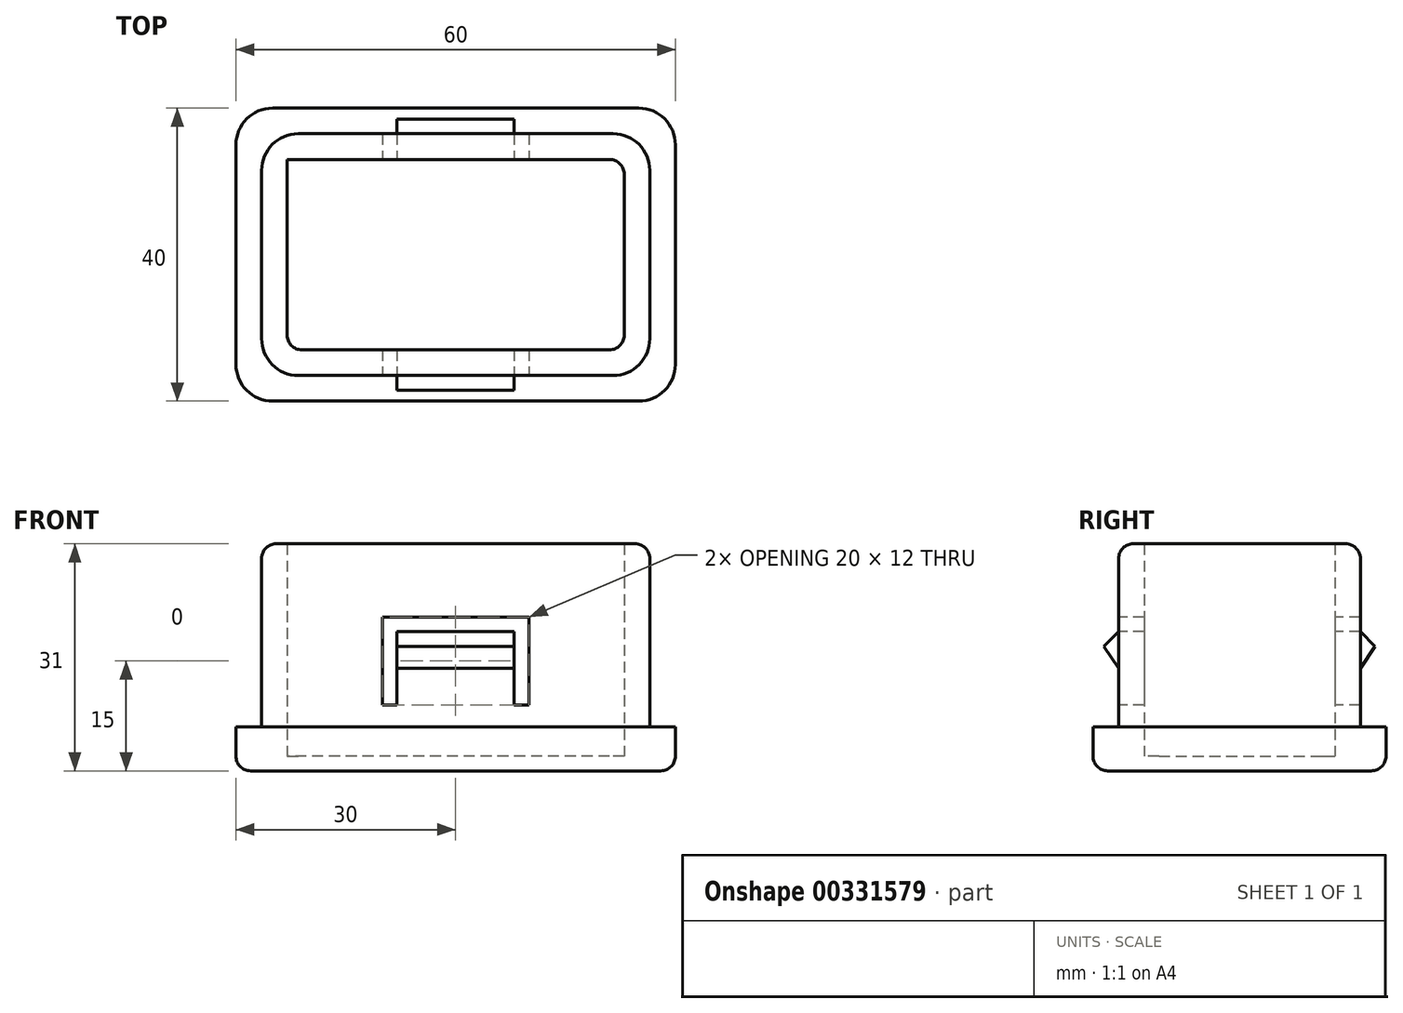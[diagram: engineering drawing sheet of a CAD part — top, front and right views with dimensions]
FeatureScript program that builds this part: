
annotation { "Feature Type Name" : "Feature", "Feature Type Description" : "" }
export const myFeature = defineFeature(function(context is Context, id is Id, definition is map)
    precondition{}
    {
        {
            var Q0;
            Q0=qCreatedBy(makeId("Top.planeOp"),FACE);
            var sketch = newSketch(context, id + "F0", { "sketchPlane" : qUnion([Q0])});
            skLineSegment(sketch, "E0.bottom", {"start": v(30, -20) * mm, "end": v(-30, -20) * mm});
            skLineSegment(sketch, "E0.top", {"start": v(30, 20) * mm, "end": v(-30, 20) * mm});
            skLineSegment(sketch, "E0.left", {"start": v(30, -20) * mm, "end": v(30, 20) * mm});
            skLineSegment(sketch, "E0.right", {"start": v(-30, -20) * mm, "end": v(-30, 20) * mm});
            skPoint(sketch, "E0.middle", {"position": v(0, 0) * mm});
            skSolve(sketch);
        }
        {
            var Q0;
            Q0 = qSketchRegion(id + "F0", true);
            extrude(context, id + "F1", {"entities" : qUnion([Q0]), "depth" : 2 * mm});
        }
        {
            var Q0;
            Q0=makeQuery(id+"F1.opExtrude","CAP_FACE",FACE,{"disambiguationData":[OSD([sQuery(id+"F0.wireOp",EDGE,"E0.bottom"),sQuery(id+"F0.wireOp",EDGE,"E0.top"),sQuery(id+"F0.wireOp",EDGE,"E0.left"),sQuery(id+"F0.wireOp",EDGE,"E0.right")])],"isStart":false});
            var sketch = newSketch(context, id + "F2", { "sketchPlane" : qUnion([Q0])});
            skLineSegment(sketch, "E1.0", {"start": v(30, 20) * mm, "end": v(-30, 20) * mm});
            skLineSegment(sketch, "E1.1", {"start": v(-30, -20) * mm, "end": v(-30, 20) * mm});
            skLineSegment(sketch, "E1.2", {"start": v(30, -20) * mm, "end": v(-30, -20) * mm});
            skLineSegment(sketch, "E1.3", {"start": v(30, -20) * mm, "end": v(30, 20) * mm});
            skLineSegment(sketch, "E2.0", {"start": v(-23, -13) * mm, "end": v(-23, 13) * mm});
            skLineSegment(sketch, "E2.1", {"start": v(23, -13) * mm, "end": v(-23, -13) * mm});
            skLineSegment(sketch, "E2.2", {"start": v(23, -13) * mm, "end": v(23, 13) * mm});
            skLineSegment(sketch, "E2.3", {"start": v(23, 13) * mm, "end": v(-23, 13) * mm});
            skSolve(sketch);
        }
        {
            var Q0;
            Q0 = qSketchRegion(id + "F2", true);
            extrude(context, id + "F3", {"entities" : qUnion([Q0]), "operationType" : NewBodyOperationType.ADD, "depth" : 4 * mm});
        }
        {
            var Q0;
            Q0=makeQuery(id+"F3.opExtrude","CAP_FACE",FACE,{"disambiguationData":[OSD([sQuery(id+"F2.wireOp",EDGE,"E1.0"),sQuery(id+"F2.wireOp",EDGE,"E1.1"),sQuery(id+"F2.wireOp",EDGE,"E1.2"),sQuery(id+"F2.wireOp",EDGE,"E1.3"),sQuery(id+"F2.wireOp",EDGE,"E2.0"),sQuery(id+"F2.wireOp",EDGE,"E2.1"),sQuery(id+"F2.wireOp",EDGE,"E2.2"),sQuery(id+"F2.wireOp",EDGE,"E2.3")])],"isStart":false});
            var sketch = newSketch(context, id + "F4", { "sketchPlane" : qUnion([Q0])});
            skLineSegment(sketch, "E3.0", {"start": v(23, 13) * mm, "end": v(-23, 13) * mm});
            skLineSegment(sketch, "E3.1", {"start": v(23, -13) * mm, "end": v(23, 13) * mm});
            skLineSegment(sketch, "E3.2", {"start": v(23, -13) * mm, "end": v(-23, -13) * mm});
            skLineSegment(sketch, "E3.3", {"start": v(-23, -13) * mm, "end": v(-23, 13) * mm});
            skLineSegment(sketch, "E4.0", {"start": v(26.5, 16.5) * mm, "end": v(-26.5, 16.5) * mm});
            skLineSegment(sketch, "E4.1", {"start": v(26.5, -16.5) * mm, "end": v(26.5, 16.5) * mm});
            skLineSegment(sketch, "E4.2", {"start": v(26.5, -16.5) * mm, "end": v(-26.5, -16.5) * mm});
            skLineSegment(sketch, "E4.3", {"start": v(-26.5, -16.5) * mm, "end": v(-26.5, 16.5) * mm});
            skSolve(sketch);
        }
        {
            var Q0;
            Q0 = qSketchRegion(id + "F4", true);
            extrude(context, id + "F5", {"entities" : qUnion([Q0]), "operationType" : NewBodyOperationType.ADD, "depth" : 25 * mm});
        }
        {
            var Q0;
            Q0=makeQuery(id+"F5.opExtrude","SWEPT_EDGE",EDGE,{"disambiguationData":[OSD([sQuery(id+"F4.wireOp",EDGE,"E4.2"),sQuery(id+"F4.wireOp",EDGE,"E4.3")])]});
            var Q1;
            Q1=makeQuery(id+"F5.opExtrude","SWEPT_EDGE",EDGE,{"disambiguationData":[OSD([sQuery(id+"F4.wireOp",EDGE,"E4.1"),sQuery(id+"F4.wireOp",EDGE,"E4.2")])]});
            var Q2;
            Q2=makeQuery(id+"F5.opExtrude","SWEPT_EDGE",EDGE,{"disambiguationData":[OSD([sQuery(id+"F4.wireOp",EDGE,"E4.0"),sQuery(id+"F4.wireOp",EDGE,"E4.3")])]});
            var Q3;
            Q3=makeQuery(id+"F3.boolean.opBoolean","MERGE",EDGE,{"derivedFrom":[makeQuery(id+"F1.opExtrude","SWEPT_EDGE",EDGE,{"disambiguationData":[OSD([sQuery(id+"F0.wireOp",EDGE,"E0.bottom"),sQuery(id+"F0.wireOp",EDGE,"E0.right")])]}),makeQuery(id+"F3.opExtrude","SWEPT_EDGE",EDGE,{"disambiguationData":[OSD([sQuery(id+"F2.wireOp",EDGE,"E1.1"),sQuery(id+"F2.wireOp",EDGE,"E1.2")])]})]});
            var Q4;
            Q4=makeQuery(id+"F3.boolean.opBoolean","MERGE",EDGE,{"derivedFrom":[makeQuery(id+"F1.opExtrude","SWEPT_EDGE",EDGE,{"disambiguationData":[OSD([sQuery(id+"F0.wireOp",EDGE,"E0.bottom"),sQuery(id+"F0.wireOp",EDGE,"E0.left")])]}),makeQuery(id+"F3.opExtrude","SWEPT_EDGE",EDGE,{"disambiguationData":[OSD([sQuery(id+"F2.wireOp",EDGE,"E1.2"),sQuery(id+"F2.wireOp",EDGE,"E1.3")])]})]});
            var Q5;
            Q5=makeQuery(id+"F3.boolean.opBoolean","MERGE",EDGE,{"derivedFrom":[makeQuery(id+"F1.opExtrude","SWEPT_EDGE",EDGE,{"disambiguationData":[OSD([sQuery(id+"F0.wireOp",EDGE,"E0.top"),sQuery(id+"F0.wireOp",EDGE,"E0.right")])]}),makeQuery(id+"F3.opExtrude","SWEPT_EDGE",EDGE,{"disambiguationData":[OSD([sQuery(id+"F2.wireOp",EDGE,"E1.0"),sQuery(id+"F2.wireOp",EDGE,"E1.1")])]})]});
            var Q6;
            Q6=makeQuery(id+"F3.boolean.opBoolean","MERGE",EDGE,{"derivedFrom":[makeQuery(id+"F1.opExtrude","SWEPT_EDGE",EDGE,{"disambiguationData":[OSD([sQuery(id+"F0.wireOp",EDGE,"E0.top"),sQuery(id+"F0.wireOp",EDGE,"E0.left")])]}),makeQuery(id+"F3.opExtrude","SWEPT_EDGE",EDGE,{"disambiguationData":[OSD([sQuery(id+"F2.wireOp",EDGE,"E1.0"),sQuery(id+"F2.wireOp",EDGE,"E1.3")])]})]});
            var Q7;
            Q7=makeQuery(id+"F5.opExtrude","SWEPT_EDGE",EDGE,{"disambiguationData":[OSD([sQuery(id+"F4.wireOp",EDGE,"E4.0"),sQuery(id+"F4.wireOp",EDGE,"E4.1")])]});
            fillet(context, id + "F6", {"entities" : qUnion([Q0, Q1, Q2, Q3, Q4, Q5, Q6, Q7]), "radius" : 5 * mm, "tangentPropagation" : true, "allowEdgeOverflow" : false});
        }
        {
            var Q0;
            Q0=makeQuery(id+"F5.opExtrude","CAP_EDGE",EDGE,{"disambiguationData":[OSD([sQuery(id+"F4.wireOp",EDGE,"E4.0")])],"isStart":false});
            var Q1;
            Q1=makeQuery(id+"F1.opExtrude","CAP_EDGE",EDGE,{"disambiguationData":[OSD([sQuery(id+"F0.wireOp",EDGE,"E0.top")])],"isStart":true});
            var Q2;
            Q2=makeQuery(id+"F5.boolean.opBoolean","MERGE",EDGE,{"derivedFrom":[makeQuery(id+"F3.opExtrude","SWEPT_EDGE",EDGE,{"disambiguationData":[OSD([sQuery(id+"F2.wireOp",EDGE,"E2.1"),sQuery(id+"F2.wireOp",EDGE,"E2.2")])]}),makeQuery(id+"F5.opExtrude","SWEPT_EDGE",EDGE,{"disambiguationData":[OSD([sQuery(id+"F4.wireOp",EDGE,"E3.1"),sQuery(id+"F4.wireOp",EDGE,"E3.2")])]})]});
            var Q3;
            Q3=makeQuery(id+"F5.boolean.opBoolean","MERGE",EDGE,{"derivedFrom":[makeQuery(id+"F3.opExtrude","SWEPT_EDGE",EDGE,{"disambiguationData":[OSD([sQuery(id+"F2.wireOp",EDGE,"E2.0"),sQuery(id+"F2.wireOp",EDGE,"E2.1")])]}),makeQuery(id+"F5.opExtrude","SWEPT_EDGE",EDGE,{"disambiguationData":[OSD([sQuery(id+"F4.wireOp",EDGE,"E3.2"),sQuery(id+"F4.wireOp",EDGE,"E3.3")])]})]});
            var Q4;
            Q4=makeQuery(id+"F5.boolean.opBoolean","MERGE",EDGE,{"derivedFrom":[makeQuery(id+"F3.opExtrude","SWEPT_EDGE",EDGE,{"disambiguationData":[OSD([sQuery(id+"F2.wireOp",EDGE,"E2.2"),sQuery(id+"F2.wireOp",EDGE,"E2.3")])]}),makeQuery(id+"F5.opExtrude","SWEPT_EDGE",EDGE,{"disambiguationData":[OSD([sQuery(id+"F4.wireOp",EDGE,"E3.0"),sQuery(id+"F4.wireOp",EDGE,"E3.1")])]})]});
            var Q5;
            Q5=makeQuery(id+"F3.opExtrude","CAP_EDGE",EDGE,{"disambiguationData":[OSD([sQuery(id+"F2.wireOp",EDGE,"E2.2")])],"isStart":true});
            var Q6;
            Q6=makeQuery(id+"F3.opExtrude","CAP_EDGE",EDGE,{"disambiguationData":[OSD([sQuery(id+"F2.wireOp",EDGE,"E2.3")])],"isStart":true});
            var Q7;
            Q7=makeQuery(id+"F3.opExtrude","CAP_EDGE",EDGE,{"disambiguationData":[OSD([sQuery(id+"F2.wireOp",EDGE,"E2.1")])],"isStart":true});
            var Q8;
            Q8=makeQuery(id+"F3.opExtrude","CAP_EDGE",EDGE,{"disambiguationData":[OSD([sQuery(id+"F2.wireOp",EDGE,"E2.0")])],"isStart":true});
            fillet(context, id + "F7", {"entities" : qUnion([Q0, Q1, Q2, Q3, Q4, Q5, Q6, Q7, Q8]), "radius" : 2 * mm, "tangentPropagation" : true, "allowEdgeOverflow" : false});
        }
        {
            var Q0;
            Q0=makeQuery(id+"F5.opExtrude","SWEPT_FACE",FACE,{"disambiguationData":[OSD([sQuery(id+"F4.wireOp",EDGE,"E4.2")])]});
            var sketch = newSketch(context, id + "F8", { "sketchPlane" : qUnion([Q0])});
            skLineSegment(sketch, "E5.bottom", {"start": v(-10, 21) * mm, "end": v(10, 21) * mm});
            skLineSegment(sketch, "E5.top", {"start": v(-10, 9) * mm, "end": v(-8, 9) * mm});
            skLineSegment(sketch, "E5.left", {"start": v(-10, 21) * mm, "end": v(-10, 9) * mm});
            skLineSegment(sketch, "E5.right", {"start": v(10, 21) * mm, "end": v(10, 9) * mm});
            skLineSegment(sketch, "E6.0", {"start": v(-8, 19) * mm, "end": v(-8, 9) * mm});
            skLineSegment(sketch, "E6.1", {"start": v(-8, 19) * mm, "end": v(8, 19) * mm});
            skLineSegment(sketch, "E6.2", {"start": v(8, 19) * mm, "end": v(8, 9) * mm});
            skLineSegment(sketch, "E7.trimOffspring", {"start": v(8, 9) * mm, "end": v(10, 9) * mm});
            skSolve(sketch);
        }
        {
            var Q0;
            Q0 = qSketchRegion(id + "F8", true);
            extrude(context, id + "F9", {"entities" : qUnion([Q0]), "operationType" : NewBodyOperationType.REMOVE, "endBound" : BoundingType.THROUGH_ALL, "oppositeDirection" : true, "depth" : 25 * mm});
        }
        {
            var Q0;
            Q0=qCreatedBy(makeId("Right.planeOp"),FACE);
            var sketch = newSketch(context, id + "F10", { "sketchPlane" : qUnion([Q0])});
            skLineSegment(sketch, "E8.0", {"start": v(-16.5, 14) * mm, "end": v(-16.5, 19) * mm});
            skLineSegment(sketch, "E9", {"start": v(-16.5, 19) * mm, "end": v(-18.5, 17) * mm});
            skPoint(sketch, "E8.1.start.orphan", {"position": v(-13, 19) * mm});
            skPoint(sketch, "E10.orphan", {"position": v(-16.5, 29) * mm});
            skPoint(sketch, "E11.orphan", {"position": v(-16.5, 6) * mm});
            skLineSegment(sketch, "E12", {"start": v(-18.5, 17) * mm, "end": v(-16.5, 14) * mm});
            skLineSegment(sketch, "E13.MirrorCS", {"start": v(16.5, 14) * mm, "end": v(16.5, 19) * mm});
            skLineSegment(sketch, "E14.MirrorCS", {"start": v(16.5, 19) * mm, "end": v(18.5, 17) * mm});
            skLineSegment(sketch, "E15.MirrorCS", {"start": v(18.5, 17) * mm, "end": v(16.5, 14) * mm});
            skSolve(sketch);
        }
        {
            var Q0;
            Q0 = qSketchRegion(id + "F10", true);
            var Q1;
            Q1=makeQuery(id+"F9.boolean.opBoolean","COPY",FACE,{"disambiguationData":[TD([makeQuery(id+"F3.opExtrude","SWEPT_FACE",FACE,{"disambiguationData":[OSD([sQuery(id+"F2.wireOp",EDGE,"E2.1")])]})])],"derivedFrom":makeQuery(id+"F9.opExtrude","SWEPT_FACE",FACE,{"disambiguationData":[OSD([sQuery(id+"F8.wireOp",EDGE,"E6.2")])]})});
            var Q2;
            Q2=makeQuery(id+"F9.boolean.opBoolean","COPY",FACE,{"disambiguationData":[TD([makeQuery(id+"F3.opExtrude","SWEPT_FACE",FACE,{"disambiguationData":[OSD([sQuery(id+"F2.wireOp",EDGE,"E2.1")])]})])],"derivedFrom":makeQuery(id+"F9.opExtrude","SWEPT_FACE",FACE,{"disambiguationData":[OSD([sQuery(id+"F8.wireOp",EDGE,"E6.0")])]})});
            extrude(context, id + "F11", {"entities" : qUnion([Q0]), "operationType" : NewBodyOperationType.ADD, "endBound" : BoundingType.UP_TO_SURFACE, "endBoundEntityFace" : qUnion([Q1]), "depth" : 25 * mm, "hasSecondDirection" : true, "secondDirectionBound" : BoundingType.UP_TO_SURFACE, "secondDirectionOppositeDirection" : true, "secondDirectionBoundEntityFace" : qUnion([Q2]), "secondDirectionDepth" : 25 * mm});
        }
    });
